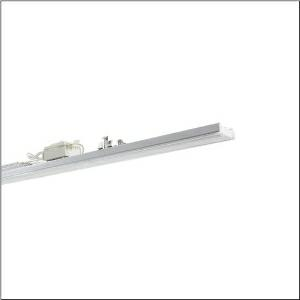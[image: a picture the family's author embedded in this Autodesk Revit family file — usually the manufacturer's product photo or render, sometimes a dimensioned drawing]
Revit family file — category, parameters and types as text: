
# Revit family: licross_11_recessed_extreme_mo_51te1edv4e5ge
name_source: partatom
category: Lighting Fixtures
units: mm (PartAtom-declared; Revit-internal decimal feet)

## family parameters
Cut with Voids When Loaded = No
Host = Face
Light Source = No
Part Type = Normal
Room Calculation Point = No
Round Connector Dimension = Use Diameter
Shared = No

## types (1)
- --- (1 x LED, 14910 lm, 84.5 W, 4000K)
    Apparent Load = 85 VA
    CIE Flux Codes = 85 95 99 100 100
    Color Rendering = 80
    Color Temperature = 4000K
    Default Elevation = 1800 mm
    Description = Licross 11 Recessed extreme MO, luminaire insert, of sheet steel, galvanised, coil coated, white, length: 2.250mm, width: 66mm, height: 67mm, LED rated luminous flux: 14.910lm, light colour: 840, SDCM (Standard Deviation of Colour Matching)MacAdam ≤ 2 SDCM (initial), control gear: DALI 2, with plug, 5-pole, with phase selection, mains connection: 220..240V, AC, 50/60Hz, rated input power: 85W, internal wiring halogen-free, primary light control with lens, of plastic, primary optical cover: cover, of PMMA, light emission: direct distribution, primary light characteristic: symmetric, protection rating (complete): IP54, insulation class (complete): insulation class I (protective earthing), certification: CE, ENEC, VDE, UKCA, protection symbol: D if used in an environment with non-conductive dust loads with corresponding accessories, impact resistance: IK06, permissible ambient temperature for indoor applications: -25..+45°C, corresponds to IFS (International Featured Standards) requirements for safety and quality in the food industry, reducing of maximum allowable ambient temperature of 5°C with ceiling mounting, LABS conformity tested according to VDMA 24364:2018-05, The light source and the operating device comply with the requirements of the Ecodesign Regulation (EU) 2019/2020 and are replaceable in accordance with this regulation, packaging unit: 1 piece
    Height = 58 mm
    Lamp = 1 x LED
    Lamp Light Flux = 14910 lm
    Lamp Power = 84.5 W
    Lamp count = 1
    Length = 2250 mm
    Luminous efficacy = 176 lm/W
    Manufacturer = Siteco
    ModVariant = No
    Model = 51TE1EDV4E5GE
    Mounting Place = Ceiling
    Mounting Type = Pendant
    Number of Poles = 1
    OnlyDefault = Yes
    Power Factor = 1
    Product Name = Licross 11 Recessed extreme MO
    Product group = luminaire insert | ceiling pendant
    ProductGroupID = 901
    Protection Class = Protection class I
    Protection Degree = IP 54
    RLX_Detail_Level = 1
    RLX_Emergency_Light_Flux = 0 lm
    RLX_Emergency_Type = 0
    RLX_Emergency_Type_DB = No
    RlxData = <blob elided: 29921 chars, md5=fed28612>
    Socket = socket
    Standby Power = 0 W
    System Light Flux = 14910 lm
    System Power = 85 W
    Type Comments = factory setting: luminous flux: 100 % | dim-lin: 254 | 380 mA
    Type Image = l_1296930.jpg
    URL = http://relux.com
    VarID = @adj_093259
    Voltage = 0 V
    Weight = 0.00 kg
    Width = 66 mm

## geometry (parser evidence)
native form markers: Blend x4, Sweep x10
no freeform markers — native parametric forms only
